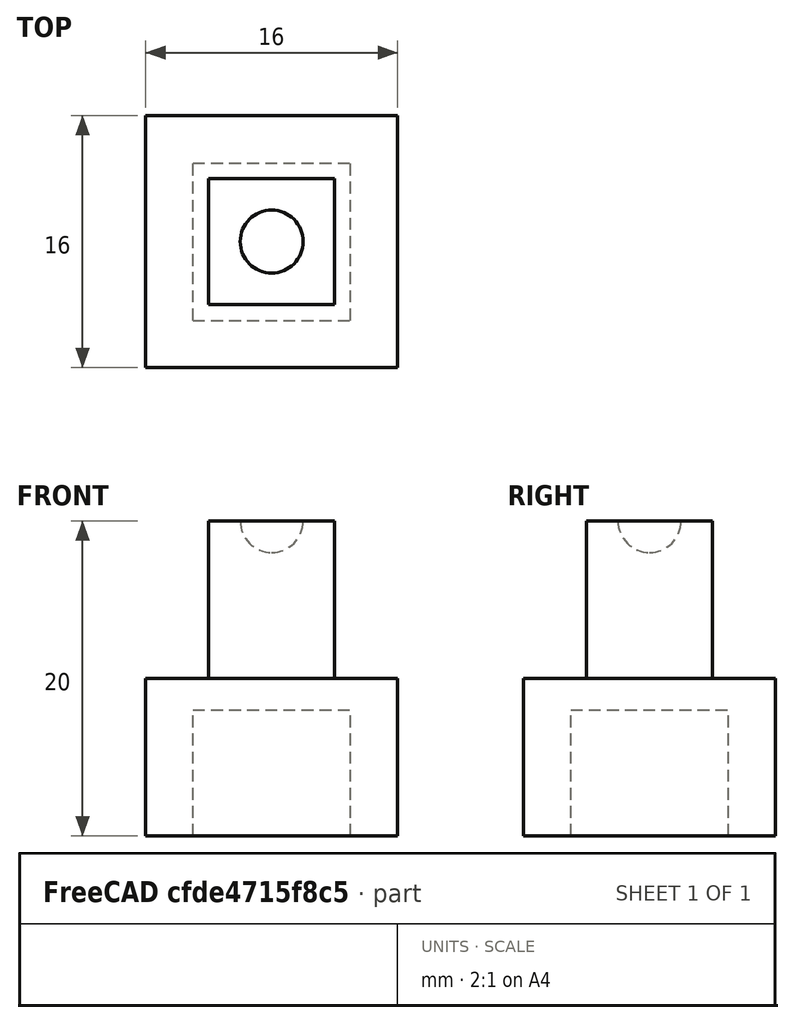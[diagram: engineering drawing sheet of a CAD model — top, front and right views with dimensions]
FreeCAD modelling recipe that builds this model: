
FCSTD DOCUMENT  (FreeCAD 0.18.3R)
Label: dot_in
License: All rights reserved
LicenseURL: http://en.wikipedia.org/wiki/All_rights_reserved
objects: Part::Box×2, PartDesign::AdditiveBox×1, PartDesign::SubtractiveSphere×1, PartDesign::Body×1, Part::Fuse×1, Part::Cut×1
note: 9 computed .brp shape members not serialized (recipe doc carries the construction recipe); baked Part::Feature solids carry a one-line shape summary decoded from their .brp

FEATURE [Part::Box] Box  label="Cube"
  AttacherType = Attacher::AttachEngine3D
  Height = 10
  Length = 16
  Placement = pos=(-8,-8,0) rot=(0,0,1;0rad)
  Width = 16
FEATURE [PartDesign::AdditiveBox] Box002
  AttacherType = Attacher::AttachEngine3D
  AttachmentOffset = pos=(-4,-4,0) rot=(0,0,1;0rad)
  Height = 20
  Length = 8
  MapMode = 5
  Placement = pos=(-4,-4,0) rot=(0,0,1;0rad)
  Support = -> [XY_Plane]
  Width = 8
FEATURE [Part::Box] Box003  label="Cube001"
  AttacherType = Attacher::AttachEngine3D
  Height = 8
  Length = 10
  Placement = pos=(-5,-5,0) rot=(0,0,1;0rad)
  Width = 10
FEATURE [PartDesign::SubtractiveSphere] Sphere
  Angle1 = -90
  Angle2 = 90
  Angle3 = 360
  AttacherType = Attacher::AttachEngine3D
  AttachmentOffset = pos=(0,0,20) rot=(0,0,1;0rad)
  BaseFeature = -> Box002
  MapMode = 5
  Placement = pos=(0,0,20) rot=(0,0,1;0rad)
  Radius = 2
  Support = -> [XY_Plane]
FEATURE [PartDesign::Body] Body
  Group = -> [Box002,Sphere]
  Origin = -> Origin
  Tip = -> Sphere
FEATURE [Part::Fuse] Fusion
  Base = -> Box
  Tool = -> Body
FEATURE [Part::Cut] Cut
  Base = -> Fusion
  Tool = -> Box003
